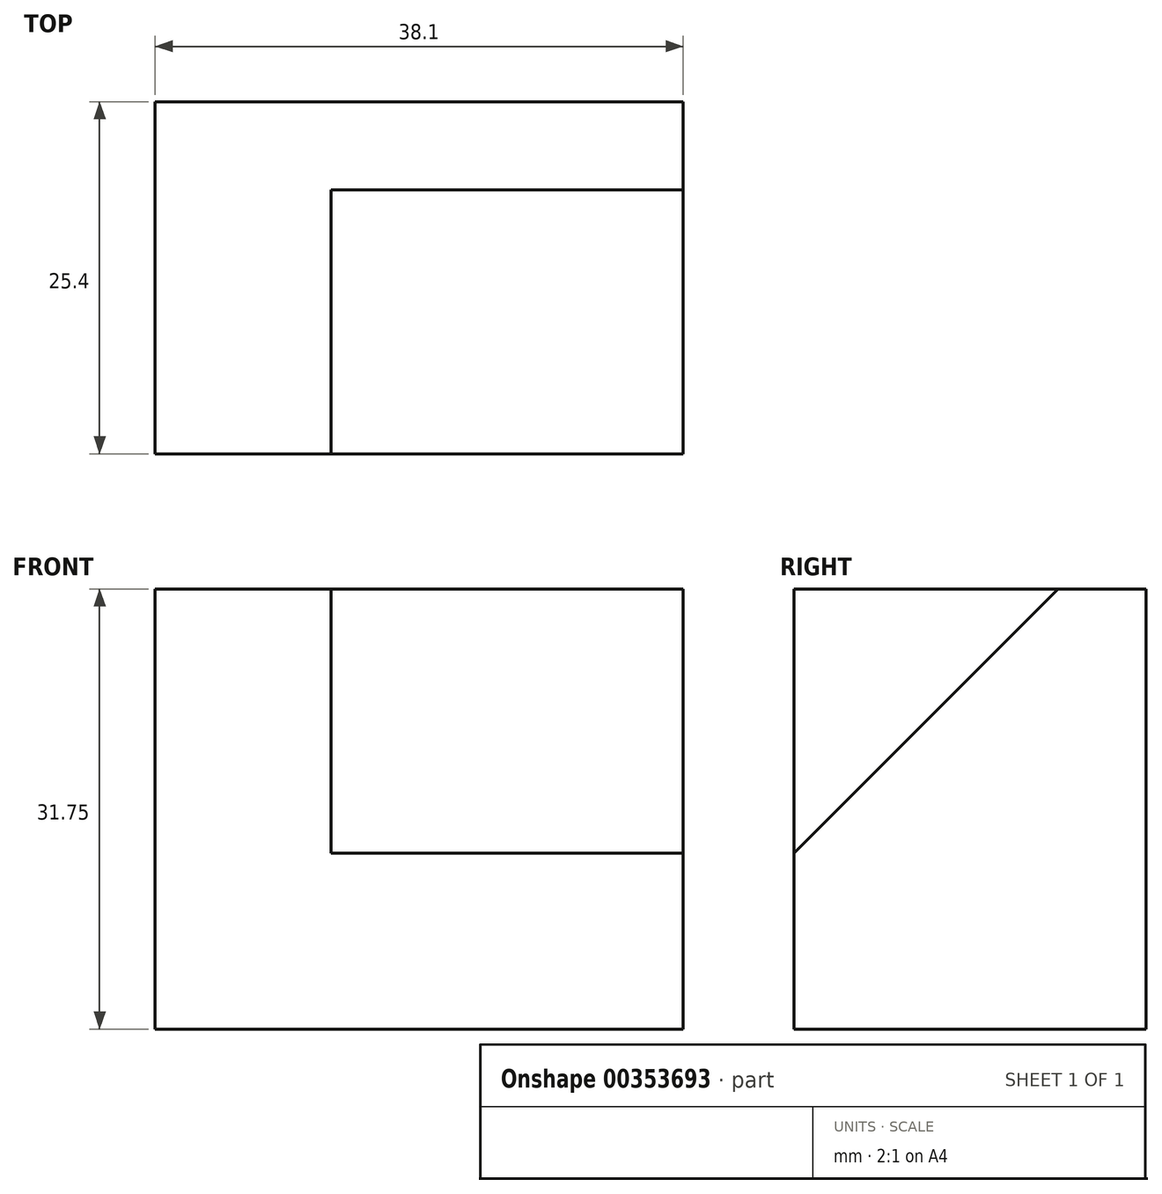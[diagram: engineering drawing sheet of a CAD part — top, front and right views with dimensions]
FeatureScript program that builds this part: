
annotation { "Feature Type Name" : "Feature", "Feature Type Description" : "" }
export const myFeature = defineFeature(function(context is Context, id is Id, definition is map)
    precondition{}
    {
        {
            var Q0;
            Q0=qCreatedBy(makeId("Front.planeOp"),FACE);
            var sketch = newSketch(context, id + "F0", { "sketchPlane" : qUnion([Q0])});
            skLineSegment(sketch, "E0", {"start": v(0, 0) * mm, "end": v(0, 31.75) * mm});
            skLineSegment(sketch, "E1", {"start": v(0, 31.75) * mm, "end": v(38.1, 31.75) * mm});
            skLineSegment(sketch, "E2", {"start": v(38.1, 31.75) * mm, "end": v(38.1, 0) * mm});
            skLineSegment(sketch, "E3", {"start": v(38.1, 0) * mm, "end": v(0, 0) * mm});
            skSolve(sketch);
        }
        {
            var Q0;
            Q0=makeQuery(id+"F0.imprint","IMPRINT",FACE,{"disambiguationData":[TD([[makeQuery(id+"F0.imprint","IMPRINT",EDGE,{"derivedFrom":sQuery(id+"F0.wireOp",EDGE,"E0")}),-1.0]])]});
            extrude(context, id + "F1", {"entities" : qUnion([Q0]), "depth" : 25.4 * mm});
        }
        {
            var Q0;
            Q0=makeQuery(id+"F1.opExtrude","SWEPT_FACE",FACE,{"disambiguationData":[OSD([sQuery(id+"F0.wireOp",EDGE,"E2")])]});
            var sketch = newSketch(context, id + "F2", { "sketchPlane" : qUnion([Q0])});
            skLineSegment(sketch, "E4", {"start": v(-25.4, 31.75) * mm, "end": v(-6.35, 31.75) * mm});
            skLineSegment(sketch, "E5", {"start": v(-6.35, 31.75) * mm, "end": v(-25.4, 12.7) * mm});
            skLineSegment(sketch, "E6", {"start": v(-25.4, 12.7) * mm, "end": v(-25.4, 31.75) * mm});
            skSolve(sketch);
        }
        {
            var Q0;
            Q0=makeQuery(id+"F2.imprint","IMPRINT",FACE,{"disambiguationData":[TD([[makeQuery(id+"F2.imprint","IMPRINT",EDGE,{"derivedFrom":sQuery(id+"F2.wireOp",EDGE,"E4")}),-1.0]])]});
            extrude(context, id + "F3", {"entities" : qUnion([Q0]), "operationType" : NewBodyOperationType.REMOVE, "oppositeDirection" : true, "depth" : 25.4 * mm});
        }
        {
            var Q0;
            Q0=makeQuery(id+"F2.imprint","IMPRINT",FACE,{"disambiguationData":[TD([[makeQuery(id+"F2.imprint","IMPRINT",EDGE,{"derivedFrom":sQuery(id+"F2.wireOp",EDGE,"E4")}),-1.0]])]});
            extrude(context, id + "F4", {"entities" : qUnion([Q0]), "operationType" : NewBodyOperationType.REMOVE, "oppositeDirection" : true, "depth" : 25.4 * mm});
        }
    });
